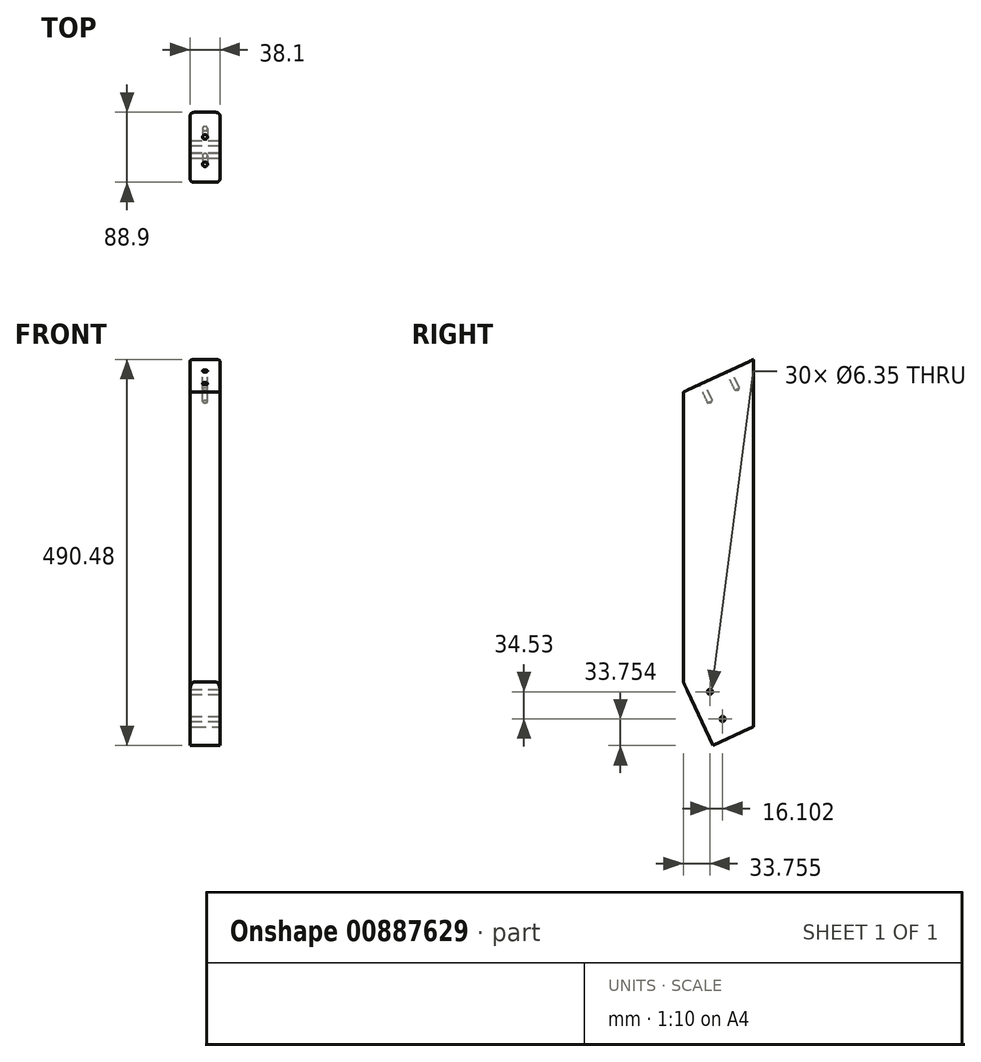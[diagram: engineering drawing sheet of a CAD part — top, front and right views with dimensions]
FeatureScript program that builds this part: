
annotation { "Feature Type Name" : "Feature", "Feature Type Description" : "" }
export const myFeature = defineFeature(function(context is Context, id is Id, definition is map)
    precondition{}
    {
        {
            var Q0;
            Q0=qCreatedBy(makeId("Top.planeOp"),FACE);
            var sketch = newSketch(context, id + "F0", { "sketchPlane" : qUnion([Q0])});
            skLineSegment(sketch, "E0.bottom", {"start": v(19.05, 44.45) * mm, "end": v(-19.05, 44.45) * mm});
            skLineSegment(sketch, "E0.top", {"start": v(19.05, -44.45) * mm, "end": v(-19.05, -44.45) * mm});
            skLineSegment(sketch, "E0.left", {"start": v(19.05, 44.45) * mm, "end": v(19.05, -44.45) * mm});
            skLineSegment(sketch, "E0.right", {"start": v(-19.05, 44.45) * mm, "end": v(-19.05, -44.45) * mm});
            skPoint(sketch, "E0.middle", {"position": v(0, 0) * mm});
            skSolve(sketch);
        }
        {
            var Q0;
            Q0=makeQuery(id+"F0.imprint","IMPRINT",FACE,{"disambiguationData":[TD([[makeQuery(id+"F0.imprint","IMPRINT",EDGE,{"derivedFrom":sQuery(id+"F0.wireOp",EDGE,"E0.bottom")}),1.0]])]});
            extrude(context, id + "F1", {"entities" : qUnion([Q0]), "endBound" : BoundingType.SYMMETRIC, "depth" : 508 * mm, "offsetDistance" : 25.4 * mm});
        }
        {
            var Q0;
            Q0=makeQuery(id+"F1.opExtrude","SWEPT_FACE",FACE,{"disambiguationData":[OSD([sQuery(id+"F0.wireOp",EDGE,"E0.left")])]});
            var sketch = newSketch(context, id + "F2", { "sketchPlane" : qUnion([Q0])});
            skLineSegment(sketch, "E1", {"start": v(-44.45, -254) * mm, "end": v(44.45, -212.55) * mm});
            skLineSegment(sketch, "E2", {"start": v(44.45, -212.55) * mm, "end": v(44.45, -254) * mm});
            skLineSegment(sketch, "E3", {"start": v(44.45, -254) * mm, "end": v(-44.45, -254) * mm});
            skLineSegment(sketch, "E4", {"start": v(-6.88, -236.48) * mm, "end": v(-44.45, -155.9) * mm});
            skLineSegment(sketch, "E5", {"start": v(-44.45, -155.9) * mm, "end": v(-44.45, -254) * mm});
            skLineSegment(sketch, "E6", {"start": v(44.45, 254) * mm, "end": v(-44.45, 212.55) * mm});
            skLineSegment(sketch, "E7", {"start": v(-44.45, 212.55) * mm, "end": v(-44.45, 254) * mm});
            skLineSegment(sketch, "E8", {"start": v(-44.45, 254) * mm, "end": v(44.45, 254) * mm});
            skSolve(sketch);
        }
        {
            var Q0;
            Q0=makeQuery(id+"F2.imprint","IMPRINT",FACE,{"disambiguationData":[TD([[makeQuery(id+"F2.imprint","IMPRINT",EDGE,{"derivedFrom":sQuery(id+"F2.wireOp",EDGE,"E6")}),-1.0]])]});
            var Q1;
            {var subQ3=sQuery(id+"F2.wireOp",EDGE,"E2");Q1=makeQuery(id+"F2.imprint","IMPRINT",FACE,{"disambiguationData":[TD([[makeQuery(id+"F2.imprint","IMPRINT",EDGE,{"derivedFrom":subQ3}),-1.0]])]});}
            var Q2;
            {var subQ2=sQuery(id+"F2.wireOp",EDGE,"E4");Q2=makeQuery(id+"F2.imprint","IMPRINT",FACE,{"disambiguationData":[TD([[makeQuery(id+"F2.imprint","IMPRINT",EDGE,{"derivedFrom":subQ2}),1.0]])]});}
            extrude(context, id + "F3", {"entities" : qUnion([Q0, Q1, Q2]), "operationType" : NewBodyOperationType.REMOVE, "endBound" : BoundingType.THROUGH_ALL, "oppositeDirection" : true, "depth" : 25.4 * mm, "offsetDistance" : 25.4 * mm});
        }
        {
            var Q0;
            Q0=makeQuery(id+"F1.opExtrude","SWEPT_FACE",FACE,{"disambiguationData":[OSD([sQuery(id+"F0.wireOp",EDGE,"E0.left")])]});
            var sketch = newSketch(context, id + "F4", { "sketchPlane" : qUnion([Q0])});
            skPoint(sketch, "E9", {"position": v(-10.7, -168.2) * mm});
            skPoint(sketch, "E9.positionSnap0", {"position": v(-25.66, -196.2) * mm});
            skPoint(sketch, "E10", {"position": v(5.4, -202.73) * mm});
            skLineSegment(sketch, "E11", {"start": v(-10.7, -168.2) * mm, "end": v(5.4, -202.73) * mm, "construction": true});
            skSolve(sketch);
        }
        {
            var Q0;
            Q0=sQuery(id+"F4.wireOp",VERTEX,"E9");
            var Q1;
            Q1=sQuery(id+"F4.wireOp",VERTEX,"E10");
            var Q2;
            Q2=makeQuery(id+"F1.opExtrude","SWEPT_BODY",BODY,{"disambiguationData":[OSD([sQuery(id+"F0.wireOp",EDGE,"E0.bottom"),sQuery(id+"F0.wireOp",EDGE,"E0.top"),sQuery(id+"F0.wireOp",EDGE,"E0.left"),sQuery(id+"F0.wireOp",EDGE,"E0.right")])]});
            hole(context, id + "F5", {"style" : HoleStyle.SIMPLE, "endStyle" : HoleEndStyle.THROUGH, "holeDiameter" : 6.35 * mm, "majorDiameter" : 6.35 * mm, "isTappedThrough" : true, "tappedDepth" : 12.7 * mm, "tapClearance" : 3, "locations" : qUnion([Q0, Q1]), "scope" : qUnion([Q2])});
        }
        {
            var Q0;
            Q0=makeQuery(id+"F1.opExtrude","SWEPT_EDGE",EDGE,{"disambiguationData":[OSD([sQuery(id+"F0.wireOp",EDGE,"E0.top"),sQuery(id+"F0.wireOp",EDGE,"E0.left")])]});
            var Q1;
            Q1=makeQuery(id+"F1.opExtrude","SWEPT_EDGE",EDGE,{"disambiguationData":[OSD([sQuery(id+"F0.wireOp",EDGE,"E0.top"),sQuery(id+"F0.wireOp",EDGE,"E0.right")])]});
            var Q2;
            Q2=makeQuery(id+"F1.opExtrude","SWEPT_EDGE",EDGE,{"disambiguationData":[OSD([sQuery(id+"F0.wireOp",EDGE,"E0.bottom"),sQuery(id+"F0.wireOp",EDGE,"E0.left")])]});
            var Q3;
            Q3=makeQuery(id+"F1.opExtrude","SWEPT_EDGE",EDGE,{"disambiguationData":[OSD([sQuery(id+"F0.wireOp",EDGE,"E0.bottom"),sQuery(id+"F0.wireOp",EDGE,"E0.right")])]});
            fillet(context, id + "F6", {"entities" : qUnion([Q0, Q1, Q2, Q3]), "radius" : 5.08 * mm, "tangentPropagation" : true, "allowEdgeOverflow" : false});
        }
        {
            var Q0;
            Q0=makeQuery(id+"F3.boolean.opBoolean","COPY",FACE,{"derivedFrom":makeQuery(id+"F3.opExtrude","SWEPT_FACE",FACE,{"disambiguationData":[OSD([sQuery(id+"F2.wireOp",EDGE,"E6")])]})});
            var sketch = newSketch(context, id + "F7", { "sketchPlane" : qUnion([Q0])});
            skPoint(sketch, "E12", {"position": v(0, 113.04) * mm});
            skPoint(sketch, "E13", {"position": v(0, 74.94) * mm});
            skSolve(sketch);
        }
        {
            var Q0;
            Q0=sQuery(id+"F7.wireOp",VERTEX,"E12");
            var Q1;
            Q1=sQuery(id+"F7.wireOp",VERTEX,"E13");
            var Q2;
            Q2=makeQuery(id+"F1.opExtrude","SWEPT_BODY",BODY,{"disambiguationData":[OSD([sQuery(id+"F0.wireOp",EDGE,"E0.bottom"),sQuery(id+"F0.wireOp",EDGE,"E0.top"),sQuery(id+"F0.wireOp",EDGE,"E0.left"),sQuery(id+"F0.wireOp",EDGE,"E0.right")])]});
            hole(context, id + "F8", {"style" : HoleStyle.SIMPLE, "endStyle" : HoleEndStyle.BLIND, "holeDiameter" : 6.35 * mm, "majorDiameter" : 6.35 * mm, "holeDepth" : 25.4 * mm, "isTappedThrough" : true, "tappedDepth" : 12.7 * mm, "tapClearance" : 3, "locations" : qUnion([Q0, Q1]), "scope" : qUnion([Q2])});
        }
    });
